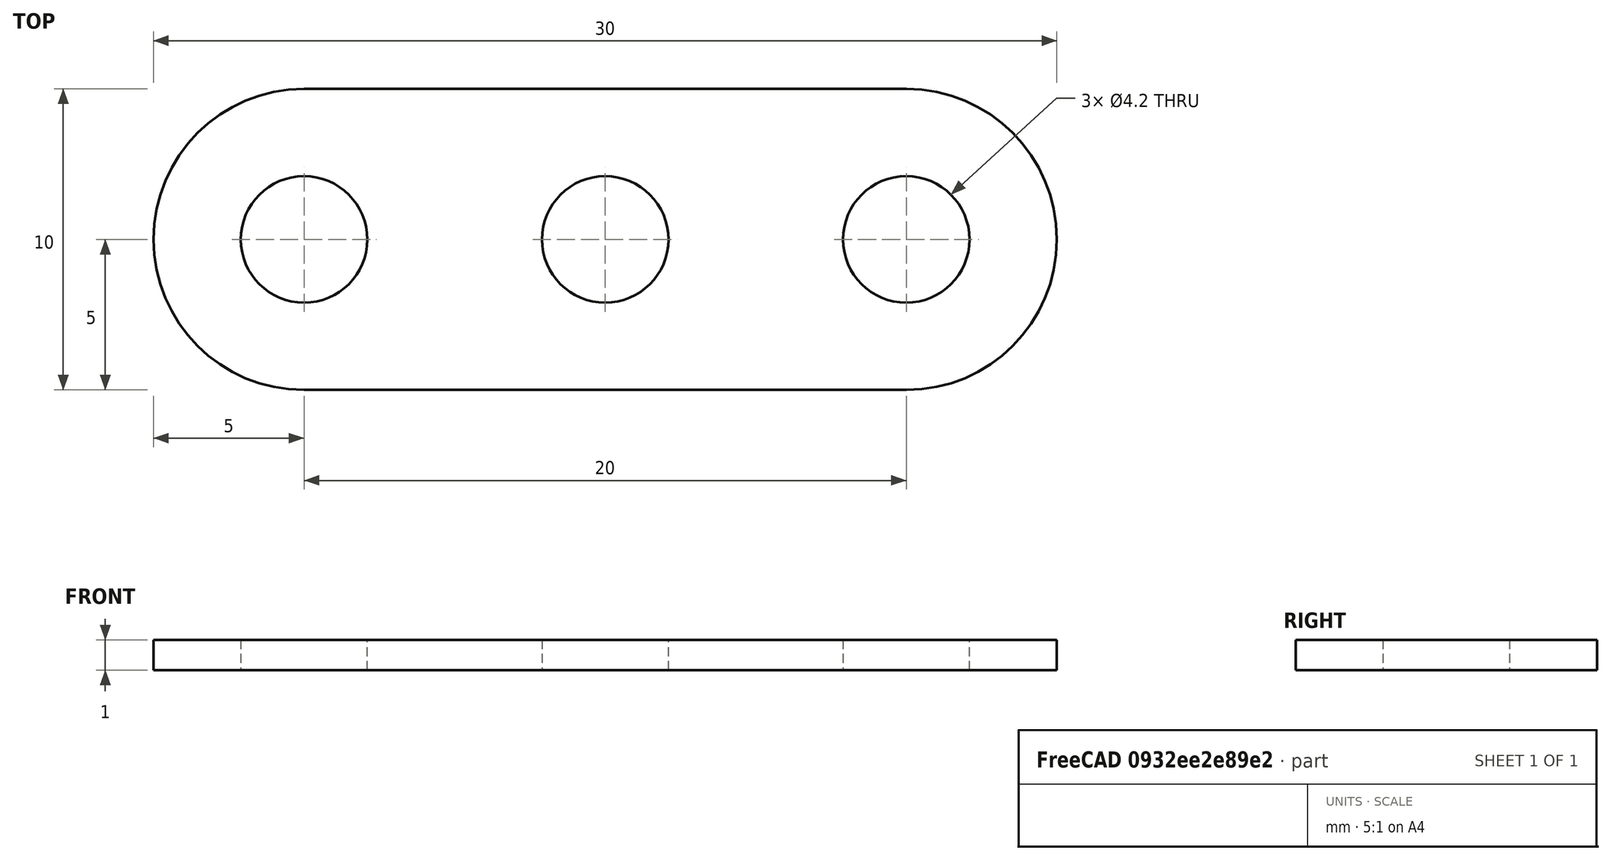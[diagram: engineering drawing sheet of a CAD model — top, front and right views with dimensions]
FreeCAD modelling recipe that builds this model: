
FCSTD DOCUMENT  (FreeCAD 0.16RUnknown)
Label: strip3
License: All rights reserved
LicenseURL: http://en.wikipedia.org/wiki/All_rights_reserved
objects: Sketcher::SketchObject×1, PartDesign::Pad×1
note: 3 computed .brp shape members not serialized (recipe doc carries the construction recipe); baked Part::Feature solids carry a one-line shape summary decoded from their .brp

FEATURE [Sketcher::SketchObject] Sketch
  sketch-geometry (9):
    g0: Circle CenterX=0 CenterY=0 CenterZ=0 NormalX=0 NormalY=0 NormalZ=1 Radius=2.1
    g1: Circle CenterX=10 CenterY=0 CenterZ=0 NormalX=0 NormalY=0 NormalZ=1 Radius=2.1
    g2: LineSegment [constr] StartX=0 StartY=0 StartZ=0 EndX=10 EndY=0 EndZ=0
    g3: Circle CenterX=20 CenterY=0 CenterZ=0 NormalX=0 NormalY=0 NormalZ=1 Radius=2.1
    g4: LineSegment [constr] StartX=10 StartY=0 StartZ=0 EndX=20 EndY=0 EndZ=0
    g5: ArcOfCircle CenterX=0 CenterY=0 CenterZ=0 NormalX=0 NormalY=0 NormalZ=1 Radius=5 StartAngle=1.5708 EndAngle=4.71239
    g6: ArcOfCircle CenterX=20 CenterY=0 CenterZ=0 NormalX=0 NormalY=0 NormalZ=1 Radius=5 StartAngle=4.71239 EndAngle=7.85398
    g7: LineSegment StartX=1e-12 StartY=-5 StartZ=0 EndX=20 EndY=-5 EndZ=0
    g8: LineSegment StartX=0 StartY=5 StartZ=0 EndX=20 EndY=5 EndZ=0
  constraints (21):
    c: Radius(g0) = 2.1
    c: Equal(g0,g1) = 5
    c: Coincident(g0,g2)
    c: Coincident(g1,g2)
    c: Equal(g0,g3) = 5
    c: Coincident(g1,g4)
    c: Coincident(g3,g4)
    c: Equal(g2,g4)
    c: Parallel(g4,g2)
    c: Coincident(g0,g-1)
    c: Distance(g-1,g1) = 10
    c: Angle(g2,g-1) = 0
    c: Tangent(g5,g8) = 1.5708
    c: Tangent(g5,g7) = -1.5708
    c: Tangent(g7,g6) = -1.5708
    c: Tangent(g8,g6) = 1.5708
    c: Horizontal(g7)
    c: Equal(g5,g6)
    c: Coincident(g-1,g5)
    c: Radius(g5) = 5
    c: Coincident(g6,g3)
FEATURE [PartDesign::Pad] Pad
  Length = 1
  Length2 = 100
  Sketch = -> Sketch
  Type = 0
